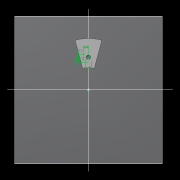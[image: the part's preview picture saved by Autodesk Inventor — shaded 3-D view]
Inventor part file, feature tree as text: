
AUTODESK INVENTOR PART (.ipt)
format: ipt  version: 2022.2 (Build 262287010, 287A)  size: 602,112 bytes
history: native  units: mm
features: extrude x27, other x19, sketch x17, pattern_circular x10, plane x5, fillet x2, move_body x2, revolve x2, draft x2, chamfer x2
ambient origin geometry x8: Origin, YZ Plane, XZ Plane, XY Plane, X Axis, Y Axis, Z Axis, Center Point
bodies: Solid5 (feature_tree)
feature tree (88):
  other  "CrossSection1"
  sketch  "Sketch7"  dims[d167=8.972256mm]
  other  "Roller1"
  other  "Roller2"
  sketch  "Sketch22"  dims[d173=10.814812mm]
  sketch  "Sketch2"  dims[d57=4.025mm d90=61.984365mm]
  sketch  "Sketch23"  dims[d201=75.0mm d232=0.0mm d233=3600.0mm]
  other  "RevRoller1"
  fillet  "Fillet1"  Radius=59.246882mm
  extrude  "Extrusion39"  Depth=61.984365mm
  pattern_circular  "Circular Pattern13"  Count=360  [1 undecoded]
  move_body  "Move Body7"
  revolve  "Revolution13"  [1 undecoded]
  fillet  "Fillet3"  Radius=0.025mm
  pattern_circular  "Circular Pattern14"  Count=24  [1 undecoded]
  move_body  "Move Body6"
  revolve  "Revolution14"  Angle=360.0deg
  other  "OuterRim_Top2"
  other  "OuterRim_Bottom2"
  plane  "Work Plane8"
  sketch  "Sketch49"  dims[d352=0.025mm]
  sketch  "Sketch50"  dims[d354=0.025mm]
  sketch  "Sketch51"  dims[d355=16.1595mm]
  extrude  "Extrusion40"  Depth=8.194mm
  extrude  "Extrusion41"  Depth=8.194mm
  extrude  "Extrusion42"  Depth=8.194mm
  extrude  "Extrusion43"  Depth=8.194mm
  sketch  "Sketch52"  dims[d356=16.159664mm]
  extrude  "Extrusion44"  Depth=8.194mm
  extrude  "Extrusion45"  TaperAngle=90.0deg  [1 undecoded]
  extrude  "Extrusion46"  Depth=8.194mm
  extrude  "Extrusion47"  Depth=8.194mm
  pattern_circular  "Circular Pattern32"  Angle=360.0deg  [1 undecoded]
  pattern_circular  "Circular Pattern33"  Angle=90.0deg  [1 undecoded]
  sketch  "Sketch57"  dims[d358=360.0deg]
  extrude  "Extrusion50"  Depth=0.1mm
  extrude  "Extrusion51"  Depth=8.194mm
  pattern_circular  "Circular Pattern34"  [2 undecoded]
  plane  "Work Plane9"
  extrude  "Extrusion52"  Depth=8.194mm
  plane  "Work Plane7"
  sketch  "Sketch47"  dims[d350=47.575427mm]
  extrude  "Rotor_Ring"  Depth=8.194mm
  draft  "FaceDraft2"
  sketch  "Sketch30"  dims[d343=16.1595mm d344=16.159664mm d345=0.025mm]
  plane  "Work Plane5"
  other  "Rotor Featurs"
  other  "RotorRim_Bottom"
  extrude  "Extrusion24"  Depth=11.193516mm
  extrude  "Extrusion25"  TaperAngle=0.0deg  [1 undecoded]
  extrude  "Extrusion26"  TaperAngle=0.0deg  [1 undecoded]
  pattern_circular  "Circular Pattern23"  [2 undecoded]
  sketch  "Sketch41"  dims[d347=0.1mm]
  extrude  "Extrusion27"  Depth=8.194mm
  extrude  "Extrusion28"  Depth=8.194mm
  pattern_circular  "Circular Pattern24"  [2 undecoded]
  extrude  "Extrusion29"  Depth=8.194mm
  extrude  "Extrusion30"  Depth=8.194mm
  extrude  "Extrusion31"  TaperAngle=90.0deg  [1 undecoded]
  pattern_circular  "Circular Pattern25"  Angle=90.0deg  [1 undecoded]
  sketch  "Sketch42"  dims[d348=0.1mm]
  extrude  "Extrusion32"  TaperAngle=90.0deg  [1 undecoded]
  extrude  "Extrusion33"  Depth=8.194mm
  extrude  "Extrusion34"  Depth=11.193516mm
  extrude  "Extrusion35"  TaperAngle=0.0deg  [1 undecoded]
  pattern_circular  "Circular Pattern26"  [2 undecoded]
  pattern_circular  "Circular Pattern27"  Count=2  [1 undecoded]
  chamfer  "Chamfer1"  Distance=2.5mm
  chamfer  "Chamfer2"  Distance=8.0mm
  draft  "FaceDraft4"
  plane  "Work Plane6"
  sketch  "Sketch43"  dims[d349=47.575591mm]
  extrude  "Extrusion37"  Depth=8.194mm
  extrude  "Extrusion38"  Depth=8.194mm TaperAngle=30.0deg
  other  "2D Equation Curve1"
  sketch  "Sketch40"  dims[d346=0.025mm]
  other  "Work Axis6"
  other  "Work Axis7"
  other  "Work Axis8"
  other  "Work Axis9"
  other  "Work Axis10"
  other  "Work Point1"
  other  "Work Point2"
  other  "Work Point3"
  other  "Work Point4"
  other  "Work Point5"
  sketch  "Sketch48"  dims[d351=0.025mm]
  sketch  "Sketch58"  dims[d359=0.5mm d360=240.0mm d361=360.0deg d363=1.308997mm d367=8.1mm d370=0.025mm d371=1.0mm d372=1.308997mm d373=90.0deg d374=0.5mm d375=240.0mm d376=360.0deg d378=90.0deg d379=0.1mm d380=0.025mm d381=0.025mm d382=0.025mm d383=0.025mm d384=11.193516mm d385=0.0mm d386=0.0mm d391=25.0mm d392=75.0mm d393=1.5mm d394=1.5mm d395=1.5mm d396=1.5mm d397=90.0deg d398=90.0deg d399=90.0deg d400=75.0mm d401=11.193516mm d402=0.0mm d486=0.436332mm d487=0.5mm d488=2.0mm d489=0.0mm d490=20.0mm d495=2.5mm d496=8.0mm d506=13.856406mm d507=55.5mm d508=8.0mm d509=0.05mm d510=2.5mm d511=30.0deg d512=12.0mm d513=6.0mm d514=0.2mm d515=30.0deg d516=131.0mm d517=65.5mm d518=0.2mm d519=100.0mm d520=120.0mm d521=2.0mm d522=150.0mm d530=50.0mm d531=5.5mm d532=5.5mm d533=5.5mm d534=85.75mm d535=73.5mm d536=61.25mm d537=24.5mm d538=3.0mm d539=2.4mm d540=0.0mm d541=0.0mm d542=0.0mm d543=5.5mm d544=3.0mm d545=0.0mm d546=90.0mm d547=360.0deg d549=3.0mm d550=3.0mm d551=2.4mm d552=0.0mm d553=5.596758mm d554=0.0mm d555=2.4mm d556=0.0mm d557=5.596758mm d558=0.0mm d559=5.596758mm d560=0.0mm d561=90.0mm d562=360.0deg d564=60.0mm d565=360.0deg d567=5.5mm d568=5.5mm d569=3.0mm d570=0.0mm d571=5.596758mm d572=0.0mm d573=3.0mm d574=0.0mm d575=5.596758mm d576=0.0mm d577=90.0mm d578=360.0deg d580=60.0mm d581=360.0deg d584=20.0mm d585=8.0mm d587=1.75mm d589=3.0mm d592=2.0mm d593=12.0mm d594=12.0mm d600=0.5mm d601=2.0mm d602=45.0deg d603=0.5mm d604=2.0mm d605=45.0deg d606=0.436332mm d607=0.5mm d608=0.0mm d609=20.0mm d611=360.0deg d613=0.0mm d614=0.0mm d617=0.99971mm d618=100.0mm d620=69.0mm d621=5.0mm d622=0.5mm d623=0.5mm d624=5.0mm d625=0.2mm d626=0.0mm d627=20.0mm d629=69.0mm d630=73.5mm d631=20.0mm d633=6.283185mm d635=5.5mm d636=3.0mm d637=7.0mm d638=4.0mm d639=5.596758mm d640=0.0mm d641=3.0mm d642=0.0mm d643=5.596758mm d644=0.0mm d645=4.0mm d646=0.0mm d647=20.0mm d649=6.283185mm d651=3.0mm d652=4.0mm d653=20.0mm d655=6.283185mm d657=7.0mm d658=5.5mm d659=5.596758mm d660=0.0mm d661=2.593516mm d662=0.0mm d663=5.596758mm d664=0.0mm d665=3.193516mm d666=0.0mm d679=50.0mm d680=360.0deg d682=50.0mm d683=360.0deg d694=6.35mm d695=6.35mm d696=6.0mm d697=6.0mm d698=11.194mm d699=0.0mm d700=8.194mm d701=0.0mm d702=60.0mm d703=360.0deg d705=4.8mm d706=-25.0mm d707=15.0deg d708=15.0deg d709=0.0mm d710=0.0mm d16=0.872665mm d17=0.872665mm d49=0.872665mm d50=0.872665mm d51=0.872665mm d52=0.872665mm d236=0.5mm d237=0.872665mm d238=0.5mm d239=0.872665mm d282=1.0mm d283=1.0mm d284=1.0mm d285=0.15mm d286=0.25mm d287=0.375mm d288=14.3117mm d289=0.75mm d290=20.594885mm d291=0.0625mm d292=0.75mm d293=0.375mm d405=0.5mm d406=0.872665mm d407=0.5mm d408=0.872665mm d413=0.5mm d414=0.872665mm d415=0.5mm d416=0.872665mm d417=0.5mm d418=0.872665mm d419=0.5mm d420=0.872665mm d421=0.872665mm d431=0.5mm d432=0.872665mm d433=0.5mm d434=0.872665mm d471=0.5mm d472=0.872665mm d473=0.5mm d474=0.872665mm d497=0.5mm d498=0.872665mm d499=0.5mm d500=0.872665mm d590=0.5mm d591=0.872665mm]
note: 21 required parameter values undecoded (feature->parameter linkage not recoverable at this tier; creation-order binding heuristic only, values carry confidence <= 0.55)